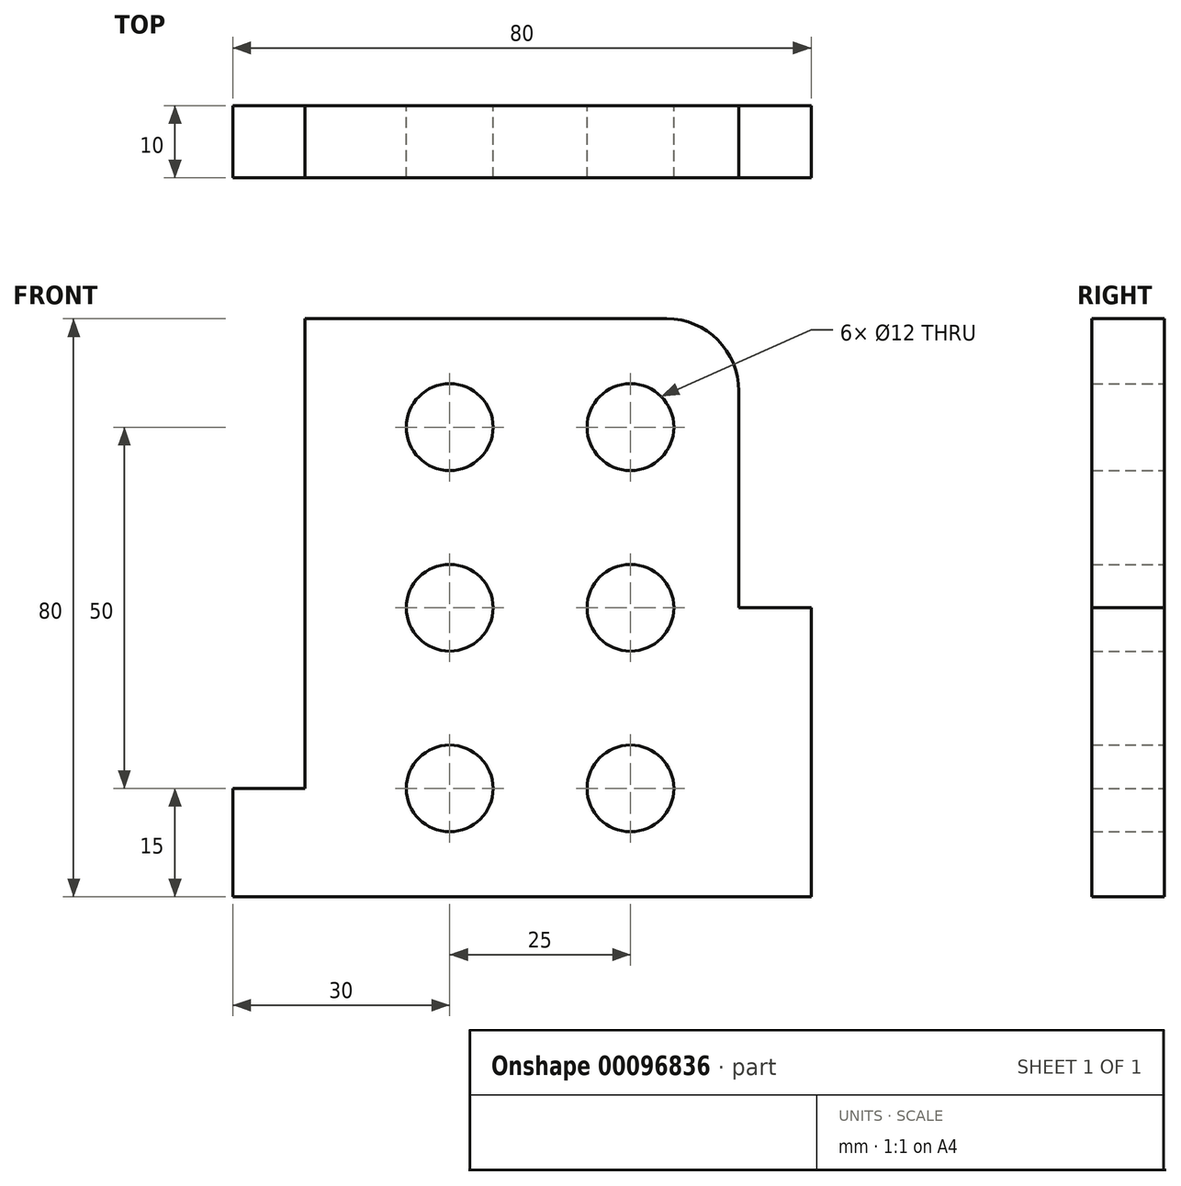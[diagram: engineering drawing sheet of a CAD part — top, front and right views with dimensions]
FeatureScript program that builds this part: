
annotation { "Feature Type Name" : "Feature", "Feature Type Description" : "" }
export const myFeature = defineFeature(function(context is Context, id is Id, definition is map)
    precondition{}
    {
        {
            var Q0;
            Q0=qCreatedBy(makeId("Front.planeOp"),FACE);
            var sketch = newSketch(context, id + "F0", { "sketchPlane" : qUnion([Q0])});
            skLineSegment(sketch, "E0", {"start": v(0, 0) * mm, "end": v(0, 15) * mm});
            skLineSegment(sketch, "E1", {"start": v(0, 15) * mm, "end": v(10, 15) * mm});
            skLineSegment(sketch, "E2", {"start": v(10, 15) * mm, "end": v(10, 80) * mm});
            skLineSegment(sketch, "E3", {"start": v(10, 80) * mm, "end": v(60, 80) * mm});
            skLineSegment(sketch, "E4", {"start": v(70, 70) * mm, "end": v(70, 40) * mm});
            skLineSegment(sketch, "E5", {"start": v(70, 40) * mm, "end": v(80, 40) * mm});
            skLineSegment(sketch, "E6", {"start": v(80, 40) * mm, "end": v(80, 0) * mm});
            skLineSegment(sketch, "E7", {"start": v(80, 0) * mm, "end": v(0, 0) * mm});
            skLineSegment(sketch, "E8", {"start": v(0, 0) * mm, "end": v(30, 0) * mm, "construction": true});
            skLineSegment(sketch, "E9", {"start": v(30, 0) * mm, "end": v(55, 0) * mm, "construction": true});
            skLineSegment(sketch, "E10", {"start": v(55, 0) * mm, "end": v(55, 15) * mm, "construction": true});
            skLineSegment(sketch, "E11", {"start": v(55, 15) * mm, "end": v(55, 40) * mm, "construction": true});
            skLineSegment(sketch, "E12", {"start": v(55, 40) * mm, "end": v(55, 65) * mm, "construction": true});
            skLineSegment(sketch, "E13", {"start": v(30, 0) * mm, "end": v(30, 15) * mm, "construction": true});
            skLineSegment(sketch, "E14", {"start": v(30, 15) * mm, "end": v(30, 40) * mm, "construction": true});
            skLineSegment(sketch, "E15", {"start": v(30, 40) * mm, "end": v(30, 65) * mm, "construction": true});
            skArc(sketch, "E16", {"start": v(70, 70) * mm, "mid": v(67.07, 77.07) * mm, "end": v(60, 80) * mm});
            skCircle(sketch, "E17", {"center": v(30, 65) * mm, "radius": 6 * mm});
            skCircle(sketch, "E18", {"center": v(55, 65) * mm, "radius": 6 * mm});
            skCircle(sketch, "E19", {"center": v(30, 40) * mm, "radius": 6 * mm});
            skCircle(sketch, "E20", {"center": v(55, 40) * mm, "radius": 6 * mm});
            skCircle(sketch, "E21", {"center": v(30, 15) * mm, "radius": 6 * mm});
            skCircle(sketch, "E22", {"center": v(55, 15) * mm, "radius": 6 * mm});
            skSolve(sketch);
        }
        {
            var Q0;
            Q0 = qSketchRegion(id + "F0", true);
            extrude(context, id + "F1", {"entities" : qUnion([Q0]), "depth" : 10 * mm});
        }
    });
